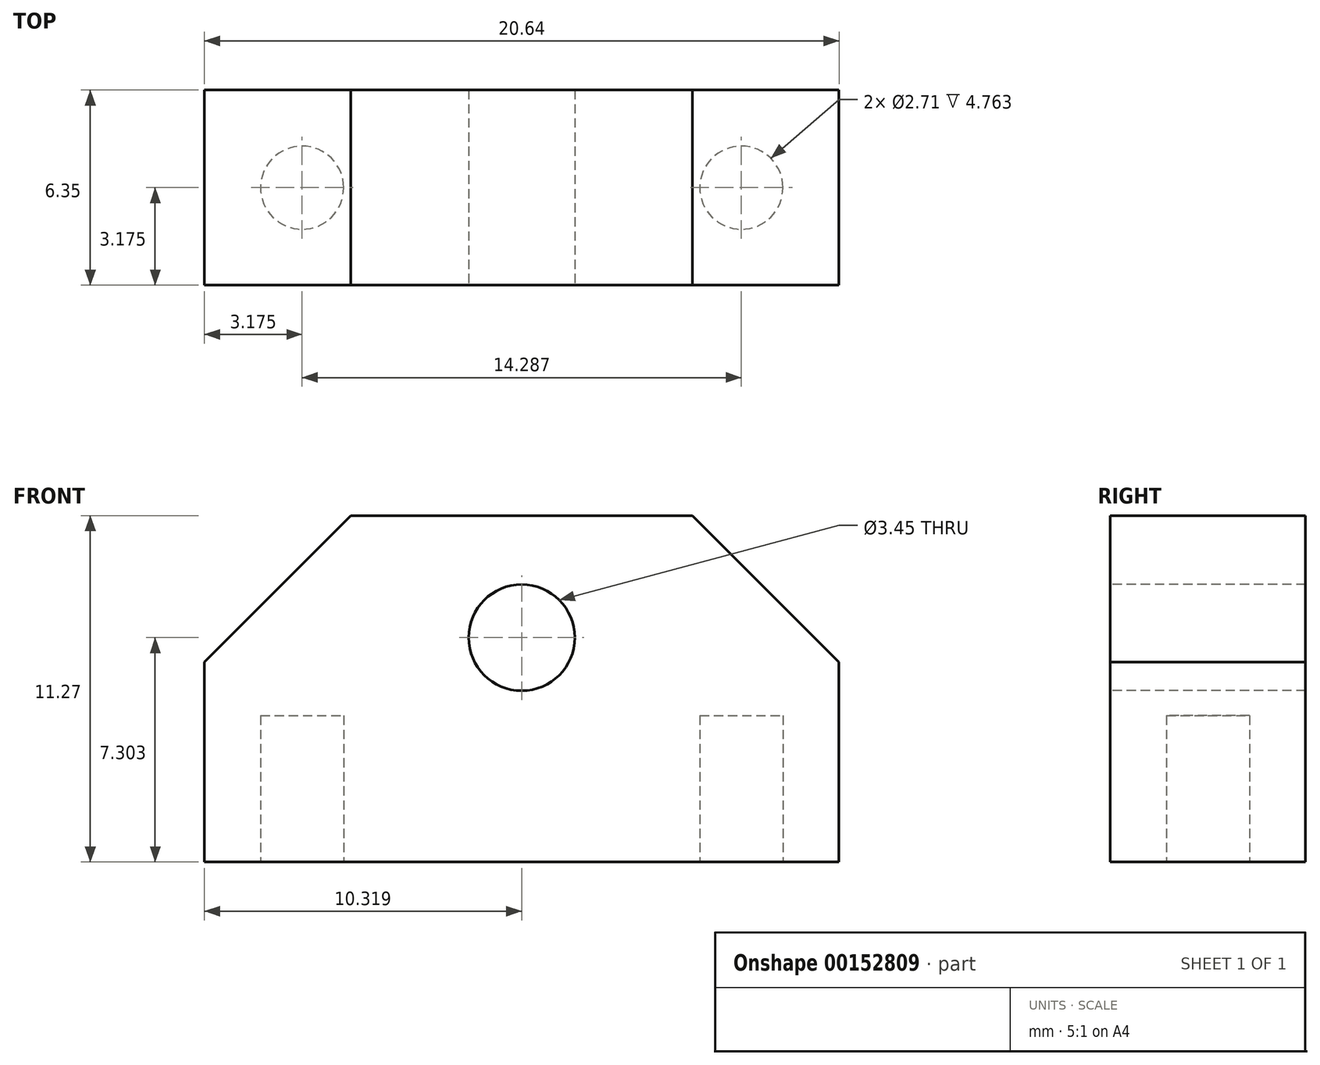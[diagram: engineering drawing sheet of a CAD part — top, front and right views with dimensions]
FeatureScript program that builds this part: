
annotation { "Feature Type Name" : "Feature", "Feature Type Description" : "" }
export const myFeature = defineFeature(function(context is Context, id is Id, definition is map)
    precondition{}
    {
        {
            var Q0;
            Q0=qCreatedBy(makeId("Top.planeOp"),FACE);
            var sketch = newSketch(context, id + "F0", { "sketchPlane" : qUnion([Q0])});
            skLineSegment(sketch, "E0.bottom", {"start": v(0, 0) * mm, "end": v(20.64, 0) * mm});
            skLineSegment(sketch, "E0.top", {"start": v(0, 6.35) * mm, "end": v(20.64, 6.35) * mm});
            skLineSegment(sketch, "E0.left", {"start": v(0, 0) * mm, "end": v(0, 6.35) * mm});
            skLineSegment(sketch, "E0.right", {"start": v(20.64, 0) * mm, "end": v(20.64, 6.35) * mm});
            skLineSegment(sketch, "E1", {"start": v(0, 3.17) * mm, "end": v(3.18, 3.17) * mm, "construction": true});
            skLineSegment(sketch, "E2", {"start": v(20.64, 3.17) * mm, "end": v(17.46, 3.17) * mm, "construction": true});
            skLineSegment(sketch, "E3", {"start": v(3.18, 3.17) * mm, "end": v(3.18, 6.35) * mm, "construction": true});
            skCircle(sketch, "E4", {"center": v(3.18, 3.17) * mm, "radius": 1.35 * mm, "construction": true});
            skCircle(sketch, "E5", {"center": v(17.46, 3.17) * mm, "radius": 1.35 * mm, "construction": true});
            skSolve(sketch);
        }
        {
            var Q0;
            Q0=qSketchRegion(id+"F0",true);
            extrude(context, id + "F1", {"entities" : qUnion([Q0]), "depth" : 11.27 * mm});
        }
        {
            var Q0;
            Q0=makeQuery(id+"F1.opExtrude","SWEPT_FACE",FACE,{"disambiguationData":[OSD([sQuery(id+"F0.wireOp",EDGE,"E0.bottom")])]});
            var sketch = newSketch(context, id + "F2", { "sketchPlane" : qUnion([Q0])});
            skLineSegment(sketch, "E6", {"start": v(10.32, 0) * mm, "end": v(10.32, 7.3) * mm, "construction": true});
            skCircle(sketch, "E7", {"center": v(10.32, 7.3) * mm, "radius": 1.73 * mm});
            skSolve(sketch);
        }
        {
            var Q0;
            Q0=qSketchRegion(id+"F2",true);
            var Q1;
            Q1=makeQuery(id+"F1.opExtrude","SWEPT_FACE",FACE,{"disambiguationData":[OSD([sQuery(id+"F0.wireOp",EDGE,"E0.top")])]});
            extrude(context, id + "F3", {"entities" : qUnion([Q0]), "operationType" : NewBodyOperationType.REMOVE, "endBound" : BoundingType.UP_TO_SURFACE, "oppositeDirection" : true, "endBoundEntityFace" : qUnion([Q1]), "depth" : 25.4 * mm});
        }
        {
            var Q0;
            Q0=makeQuery(id+"F1.opExtrude","CAP_FACE",FACE,{"disambiguationData":[OSD([sQuery(id+"F0.wireOp",EDGE,"E0.bottom"),sQuery(id+"F0.wireOp",EDGE,"E0.top"),sQuery(id+"F0.wireOp",EDGE,"E0.left"),sQuery(id+"F0.wireOp",EDGE,"E0.right")])],"isStart":true});
            var sketch = newSketch(context, id + "F4", { "sketchPlane" : qUnion([Q0])});
            skLineSegment(sketch, "E8.bottom", {"start": v(20.64, -3.17) * mm, "end": v(17.46, -3.17) * mm, "construction": true});
            skLineSegment(sketch, "E8.top", {"start": v(20.64, 0) * mm, "end": v(17.46, 0) * mm, "construction": true});
            skLineSegment(sketch, "E8.left", {"start": v(20.64, -3.17) * mm, "end": v(20.64, 0) * mm, "construction": true});
            skLineSegment(sketch, "E8.right", {"start": v(17.46, -3.18) * mm, "end": v(17.46, 0) * mm, "construction": true});
            skLineSegment(sketch, "E9.bottom", {"start": v(0, -3.17) * mm, "end": v(3.17, -3.17) * mm, "construction": true});
            skLineSegment(sketch, "E9.top", {"start": v(0, 0) * mm, "end": v(3.17, 0) * mm, "construction": true});
            skLineSegment(sketch, "E9.left", {"start": v(0, -3.17) * mm, "end": v(0, 0) * mm, "construction": true});
            skLineSegment(sketch, "E9.right", {"start": v(3.17, -3.18) * mm, "end": v(3.17, 0) * mm, "construction": true});
            skCircle(sketch, "E10", {"center": v(3.17, -3.17) * mm, "radius": 1.35 * mm});
            skCircle(sketch, "E11", {"center": v(17.46, -3.17) * mm, "radius": 1.35 * mm});
            skSolve(sketch);
        }
        {
            var Q0;
            Q0=qSketchRegion(id+"F4",true);
            extrude(context, id + "F5", {"entities" : qUnion([Q0]), "operationType" : NewBodyOperationType.REMOVE, "oppositeDirection" : true, "depth" : 4.76 * mm});
        }
        {
            var Q0;
            Q0=makeQuery(id+"F1.opExtrude","CAP_EDGE",EDGE,{"disambiguationData":[OSD([sQuery(id+"F0.wireOp",EDGE,"E0.left")])],"isStart":false});
            var Q1;
            Q1=makeQuery(id+"F1.opExtrude","CAP_EDGE",EDGE,{"disambiguationData":[OSD([sQuery(id+"F0.wireOp",EDGE,"E0.right")])],"isStart":false});
            chamfer(context, id + "F6", {"entities" : qUnion([Q0, Q1]), "width" : 4.76 * mm, "tangentPropagation" : true});
        }
    });
